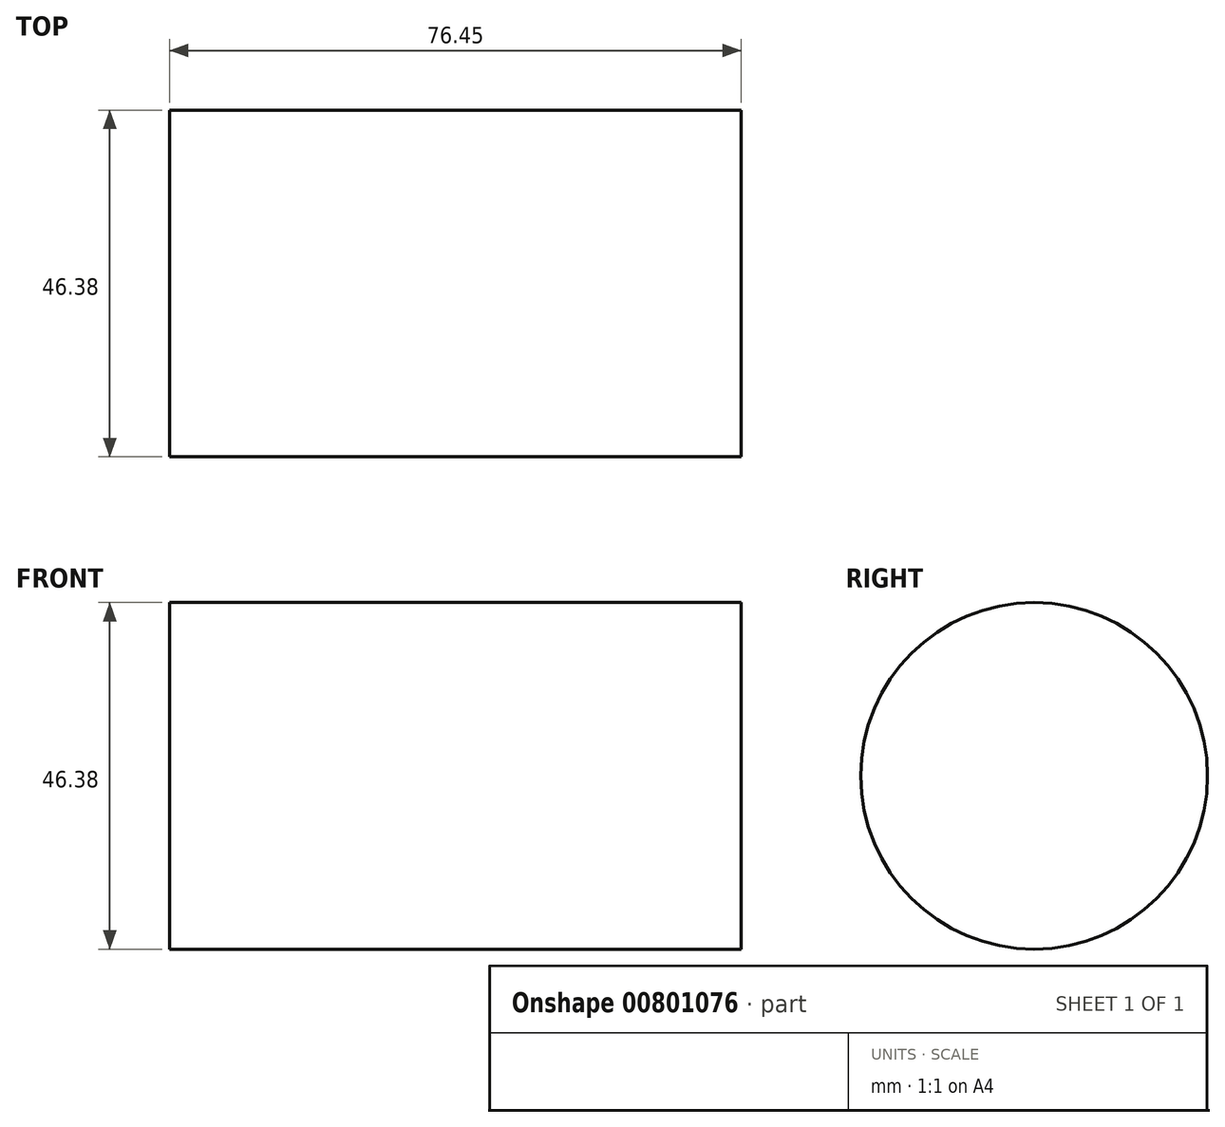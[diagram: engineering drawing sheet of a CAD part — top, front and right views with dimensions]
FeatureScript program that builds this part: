
annotation { "Feature Type Name" : "Feature", "Feature Type Description" : "" }
export const myFeature = defineFeature(function(context is Context, id is Id, definition is map)
    precondition{}
    {
        {
            var Q0;
            Q0=qCreatedBy(makeId("Right.planeOp"),FACE);
            var sketch = newSketch(context, id + "F0", { "sketchPlane" : qUnion([Q0])});
            skCircle(sketch, "E0", {"center": v(0, 0) * mm, "radius": 23.2 * mm});
            skSolve(sketch);
        }
        {
            var Q0;
            Q0=makeQuery(id+"F0.imprint","IMPRINT",FACE,{"disambiguationData":[TD([[makeQuery(id+"F0.imprint","IMPRINT",EDGE,{"derivedFrom":sQuery(id+"F0.wireOp",EDGE,"E0")}),1.0]])]});
            extrude(context, id + "F1", {"entities" : qUnion([Q0]), "depth" : 76.45 * mm, "offsetDistance" : 25.4 * mm});
        }
    });
